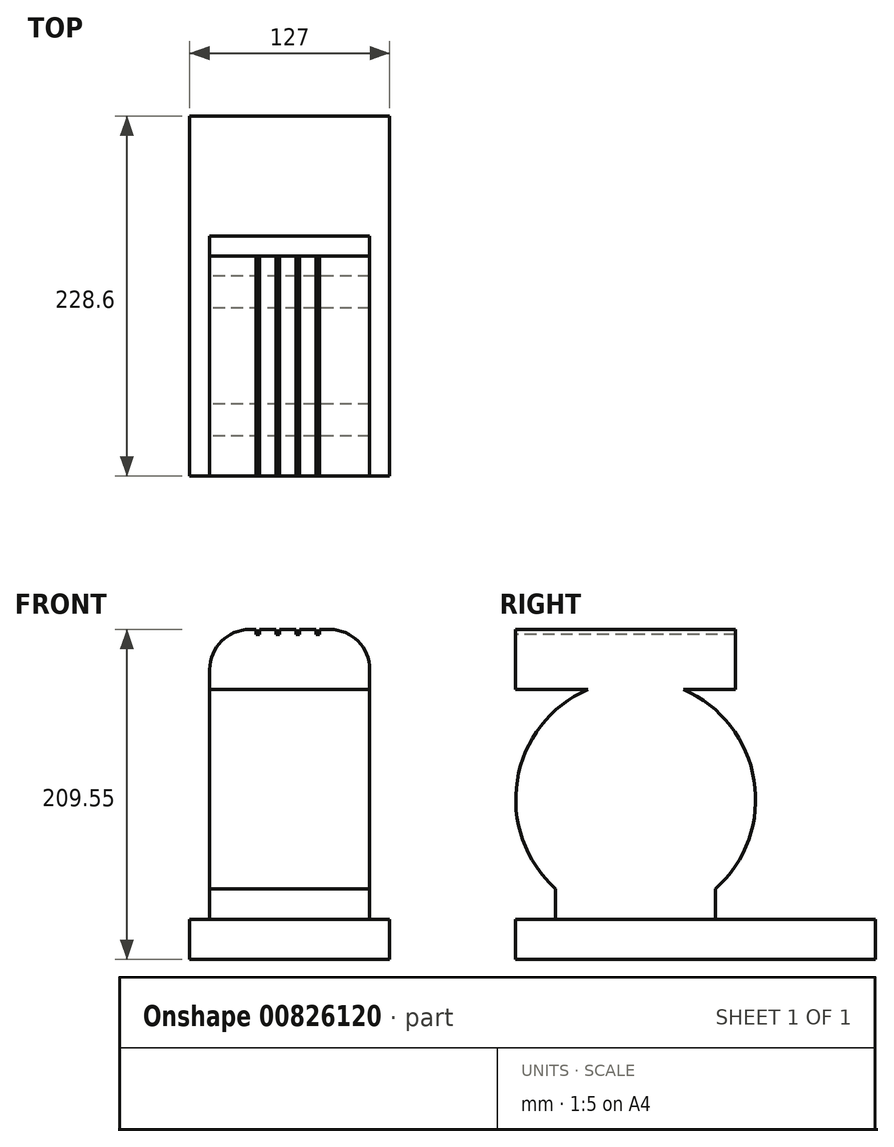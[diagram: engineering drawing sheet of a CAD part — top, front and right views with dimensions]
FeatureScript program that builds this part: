
annotation { "Feature Type Name" : "Feature", "Feature Type Description" : "" }
export const myFeature = defineFeature(function(context is Context, id is Id, definition is map)
    precondition{}
    {
        {
            var Q0;
            Q0=qCreatedBy(makeId("Right.planeOp"),FACE);
            var sketch = newSketch(context, id + "F0", { "sketchPlane" : qUnion([Q0])});
            skLineSegment(sketch, "E0.bottom", {"start": v(0, 0) * mm, "end": v(228.6, 0) * mm});
            skLineSegment(sketch, "E0.top", {"start": v(0, 25.4) * mm, "end": v(228.6, 25.4) * mm});
            skLineSegment(sketch, "E0.left", {"start": v(0, 0) * mm, "end": v(0, 25.4) * mm});
            skLineSegment(sketch, "E0.right", {"start": v(228.6, 0) * mm, "end": v(228.6, 25.4) * mm});
            skSolve(sketch);
        }
        {
            var Q0;
            Q0=qSketchRegion(id+"F0",true);
            extrude(context, id + "F1", {"entities" : qUnion([Q0]), "endBound" : BoundingType.SYMMETRIC, "depth" : 127 * mm, "offsetDistance" : 25.4 * mm});
        }
        {
            var Q0;
            Q0=qCreatedBy(makeId("Right.planeOp"),FACE);
            var sketch = newSketch(context, id + "F2", { "sketchPlane" : qUnion([Q0])});
            skArc(sketch, "E1", {"start": v(127, 44.8) * mm, "mid": v(76.2, 177.8) * mm, "end": v(25.4, 44.8) * mm});
            skLineSegment(sketch, "E2", {"start": v(127, 44.8) * mm, "end": v(127, 6.35) * mm});
            skLineSegment(sketch, "E3", {"start": v(25.4, 44.8) * mm, "end": v(25.4, 6.35) * mm});
            skLineSegment(sketch, "E4", {"start": v(127, 6.35) * mm, "end": v(25.4, 6.35) * mm});
            skSolve(sketch);
        }
        {
            var Q0;
            Q0=qSketchRegion(id+"F2",true);
            extrude(context, id + "F3", {"entities" : qUnion([Q0]), "operationType" : NewBodyOperationType.ADD, "endBound" : BoundingType.SYMMETRIC, "depth" : 101.6 * mm, "offsetDistance" : 25.4 * mm});
        }
        {
            var Q0;
            Q0=qCreatedBy(makeId("Front.planeOp"),FACE);
            var sketch = newSketch(context, id + "F4", { "sketchPlane" : qUnion([Q0])});
            skLineSegment(sketch, "E5", {"start": v(-50.8, 171.45) * mm, "end": v(50.8, 171.45) * mm});
            skLineSegment(sketch, "E6", {"start": v(0, 345.73) * mm, "end": v(0, 0) * mm, "construction": true});
            skLineSegment(sketch, "E7", {"start": v(-50.8, 171.45) * mm, "end": v(-50.8, 184.15) * mm});
            skLineSegment(sketch, "E8", {"start": v(50.8, 171.45) * mm, "end": v(50.8, 184.15) * mm});
            skLineSegment(sketch, "E9", {"start": v(-25.4, 209.55) * mm, "end": v(-21.57, 209.55) * mm});
            skPoint(sketch, "E10.visualSharp", {"position": v(-50.8, 209.55) * mm});
            skArc(sketch, "E10.filletArc", {"start": v(-25.4, 209.55) * mm, "mid": v(-43.36, 202.11) * mm, "end": v(-50.8, 184.15) * mm});
            skPoint(sketch, "E11.visualSharp", {"position": v(50.8, 209.55) * mm});
            skArc(sketch, "E11.filletArc", {"start": v(50.8, 184.15) * mm, "mid": v(43.36, 202.11) * mm, "end": v(25.4, 209.55) * mm});
            skLineSegment(sketch, "E12.top", {"start": v(18.87, 206.38) * mm, "end": v(16.53, 206.38) * mm});
            skLineSegment(sketch, "E12.left", {"start": v(18.87, 209.55) * mm, "end": v(18.87, 206.38) * mm});
            skLineSegment(sketch, "E12.right", {"start": v(16.53, 209.55) * mm, "end": v(16.53, 206.38) * mm});
            skLineSegment(sketch, "E13.top", {"start": v(6.17, 206.38) * mm, "end": v(3.83, 206.38) * mm});
            skLineSegment(sketch, "E13.left", {"start": v(6.17, 209.55) * mm, "end": v(6.17, 206.38) * mm});
            skLineSegment(sketch, "E13.right", {"start": v(3.83, 209.55) * mm, "end": v(3.83, 206.38) * mm});
            skLineSegment(sketch, "E14.top", {"start": v(-6.53, 206.38) * mm, "end": v(-8.87, 206.38) * mm});
            skLineSegment(sketch, "E14.left", {"start": v(-6.53, 209.55) * mm, "end": v(-6.53, 206.38) * mm});
            skLineSegment(sketch, "E14.right", {"start": v(-8.87, 209.55) * mm, "end": v(-8.87, 206.38) * mm});
            skLineSegment(sketch, "E15.top", {"start": v(-19.23, 206.38) * mm, "end": v(-21.57, 206.38) * mm});
            skLineSegment(sketch, "E15.left", {"start": v(-19.23, 209.55) * mm, "end": v(-19.23, 206.38) * mm});
            skLineSegment(sketch, "E15.right", {"start": v(-21.57, 209.55) * mm, "end": v(-21.57, 206.38) * mm});
            skLineSegment(sketch, "E16.trimOffspring", {"start": v(18.87, 209.55) * mm, "end": v(25.4, 209.55) * mm});
            skLineSegment(sketch, "E17.trimOffspring", {"start": v(6.17, 209.55) * mm, "end": v(16.53, 209.55) * mm});
            skLineSegment(sketch, "E18.trimOffspring", {"start": v(-6.53, 209.55) * mm, "end": v(3.83, 209.55) * mm});
            skLineSegment(sketch, "E19.trimOffspring", {"start": v(-19.23, 209.55) * mm, "end": v(-8.87, 209.55) * mm});
            skSolve(sketch);
        }
        {
            var Q0;
            Q0=makeQuery(id+"F4.imprint","IMPRINT",FACE,{"disambiguationData":[TD([[makeQuery(id+"F4.imprint","IMPRINT",EDGE,{"derivedFrom":sQuery(id+"F4.wireOp",EDGE,"E5")}),1.0]])]});
            extrude(context, id + "F5", {"entities" : qUnion([Q0]), "operationType" : NewBodyOperationType.ADD, "oppositeDirection" : true, "depth" : 139.7 * mm, "offsetDistance" : 25.4 * mm});
        }
    });
